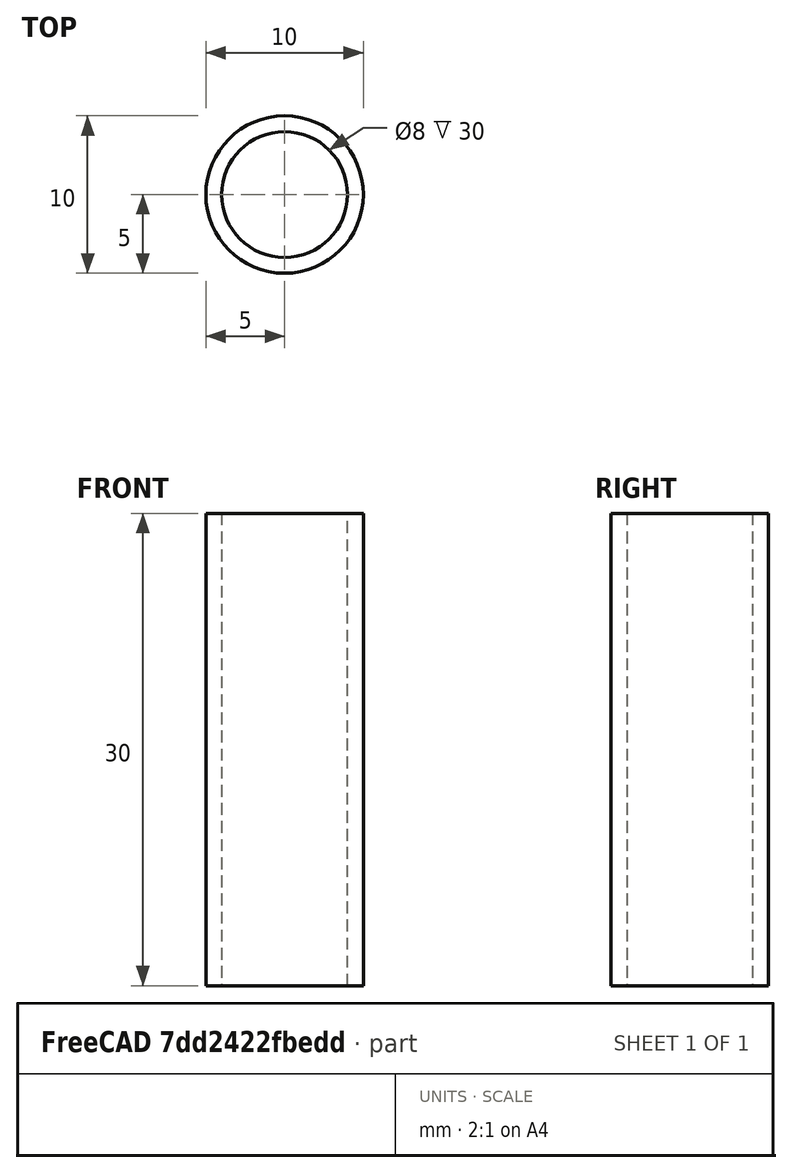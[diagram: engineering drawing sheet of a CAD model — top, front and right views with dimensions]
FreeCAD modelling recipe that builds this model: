
FCSTD DOCUMENT  (FreeCAD 0.19R24276 (Git))
Label: Trubka
License: All rights reserved
LicenseURL: http://en.wikipedia.org/wiki/All_rights_reserved
objects: Sketcher::SketchObject×1, PartDesign::Pad×1, PartDesign::Body×1
note: 4 computed .brp shape members not serialized (recipe doc carries the construction recipe); baked Part::Feature solids carry a one-line shape summary decoded from their .brp

FEATURE [Sketcher::SketchObject] Sketch
  FullyConstrained = true
  MapMode = 5
  Support = -> [XY_Plane]
  sketch-geometry (2):
    g0: Circle CenterX=0 CenterY=0 CenterZ=0 NormalX=0 NormalY=0 NormalZ=1 AngleXU=0 Radius=4
    g1: Circle CenterX=0 CenterY=0 CenterZ=0 NormalX=0 NormalY=0 NormalZ=1 AngleXU=0 Radius=5
  constraints (4):
    c: Coincident(g0,g-1)
    c: Coincident(g1,g0)
    c: Diameter(g1) = 10
    c: Diameter(g0) = 8
FEATURE [PartDesign::Pad] Pad
  Direction = (1,1,1)
  Length = 30
  Length2 = 100
  Profile = -> Sketch
  Type = 0
FEATURE [PartDesign::Body] Body
  Group = -> [Sketch,Pad]
  Origin = -> Origin
  Tip = -> Pad
